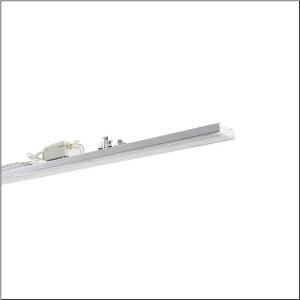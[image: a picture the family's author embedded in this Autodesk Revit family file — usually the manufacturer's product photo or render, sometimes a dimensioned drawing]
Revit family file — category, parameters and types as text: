
# Revit family: licross_r__21_recessed_mo_52tl12dn195g_f2ff
name_source: partatom
category: Lighting Fixtures
units: mm (PartAtom-declared; Revit-internal decimal feet)

## family parameters
Cut with Voids When Loaded = No
Host = Face
Light Source = No
Part Type = Normal
Room Calculation Point = No
Round Connector Dimension = Use Diameter
Shared = No

## types (1)
- --- (1 x LED, 9950 lm, 58 W, 3500K)
    Apparent Load = 58 VA
    CIE Flux Codes = 72 92 99 100 100
    Color Rendering = 80
    Color Temperature = 3500K
    Default Elevation = 1800 mm
    Description = Licross® 21 Recessed MO, luminaire insert, of sheet steel, galvanised, coil coated, white, length: 1.500mm, width: 66mm, height: 67mm, LED rated luminous flux: 9.950lm, light colour: 835, control gear: DALI 2, with plug, 5-pole, with phase selection, mains connection: 220..240V, AC, 50/60Hz, rated input power: 58W, halogen-free wiring, primary optical cover: cover, of PMMA, light emission: direct distribution, primary light characteristic: symmetric, protection rating (complete): IP40, insulation class (complete): insulation class I (protective earthing), certification: CE, ENEC, VDE, UKCA, protection symbol: D if used in an environment without relevant dust loads with corresponding accessories, impact resistance: IK06, permissible ambient temperature for indoor applications: -25..+35°C, corresponds to IFS (International Featured Standards) requirements for safety and quality in the food industry, reducing of maximum allowable ambient temperature of 5°C with ceiling mounting, LABS conformity tested according to VDMA 24364:2018-05, packaging unit: 1 piece
    Height = 58 mm
    Lamp = 1 x LED
    Lamp Light Flux = 9950 lm
    Lamp Power = 58 W
    Lamp count = 1
    Length = 1500 mm
    Luminous efficacy = 172 lm/W
    Manufacturer = Siteco
    ModVariant = No
    Model = 52TL12DN195G
    Mounting Place = Ceiling
    Mounting Type = Pendant
    Number of Poles = 1
    OnlyDefault = Yes
    Power Factor = 1
    Product Name = Licross® 21 Recessed MO
    Product group = luminaire insert
    ProductGroupID = 901
    Protection Class = Protection class I
    Protection Degree = IP 40
    RLX_Detail_Level = 1
    RLX_Emergency_Light_Flux = 0 lm
    RLX_Emergency_Type = 0
    RLX_Emergency_Type_DB = No
    RlxData = <blob elided: 24561 chars, md5=8210aa78>
    Socket = socket
    Standby Power = 0 W
    System Light Flux = 9950 lm
    System Power = 58 W
    Type Comments = factory setting: luminous flux: 100 % | dim-lin: 254 | 390 mA
    Type Image = l_1296930.jpg
    URL = http://relux.com
    VarID = @adj_058461
    Voltage = 0 V
    Weight = 0.00 kg
    Width = 66 mm

## geometry (parser evidence)
native form markers: Blend x4, Sweep x12
no freeform markers — native parametric forms only
